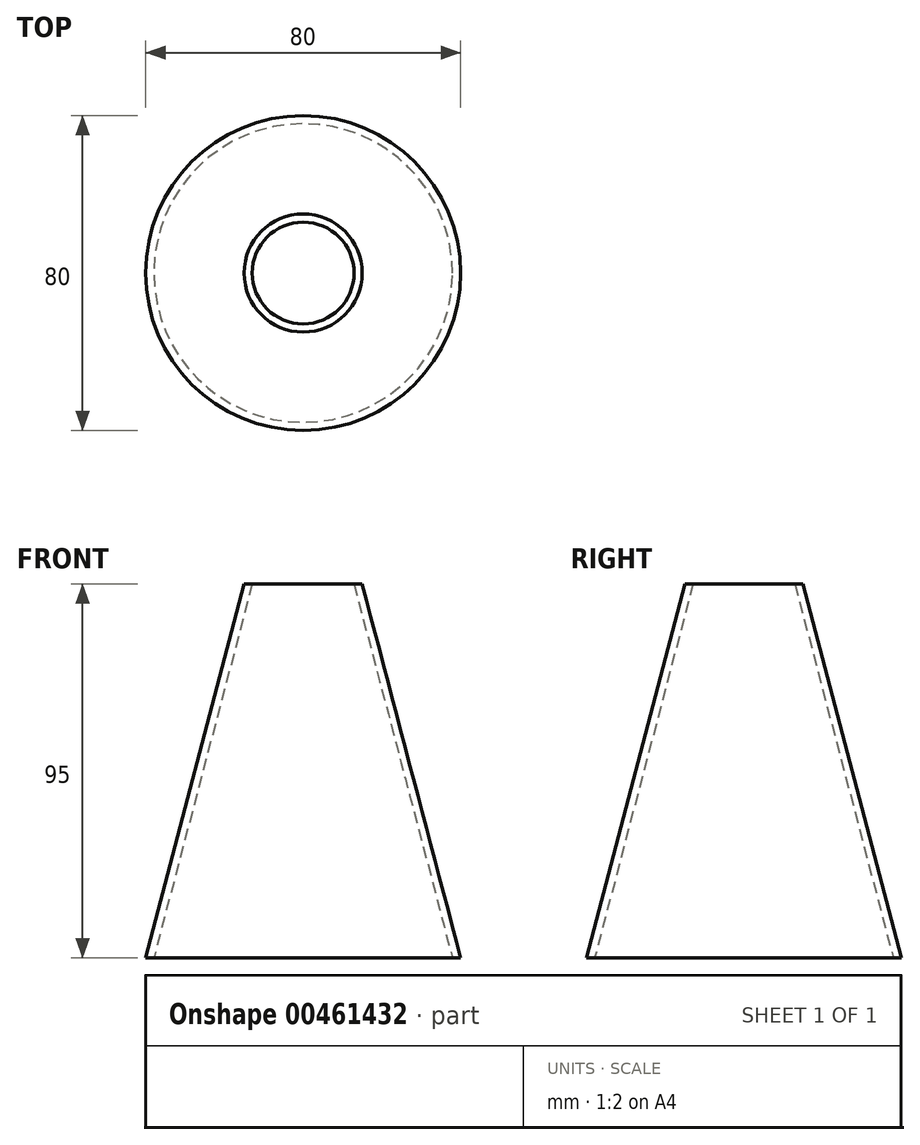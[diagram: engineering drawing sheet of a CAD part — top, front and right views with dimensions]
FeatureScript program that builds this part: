
annotation { "Feature Type Name" : "Feature", "Feature Type Description" : "" }
export const myFeature = defineFeature(function(context is Context, id is Id, definition is map)
    precondition{}
    {
        {
            var Q0;
            Q0=qCreatedBy(makeId("Top.planeOp"),FACE);
            var sketch = newSketch(context, id + "F0", { "sketchPlane" : qUnion([Q0])});
            skCircle(sketch, "E0", {"center": v(0, 0) * mm, "radius": 40 * mm});
            skSolve(sketch);
        }
        {
            var Q0;
            Q0=qCreatedBy(makeId("Top.planeOp"),FACE);
            cPlane(context, id + "F1", {"entities" : qUnion([Q0]), "cplaneType" : CPlaneType.OFFSET, "offset" : 95 * mm, "width" : 150 * mm, "height" : 150 * mm});
        }
        {
            var Q0;
            Q0=qCreatedBy(id+"F1.planeOp",FACE);
            var sketch = newSketch(context, id + "F2", { "sketchPlane" : qUnion([Q0])});
            skCircle(sketch, "E1", {"center": v(0, 0) * mm, "radius": 15 * mm});
            skSolve(sketch);
        }
        {
            var Q0;
            Q0=makeQuery(id+"F0.imprint","IMPRINT",FACE,{"disambiguationData":[TD([[makeQuery(id+"F0.imprint","IMPRINT",EDGE,{"derivedFrom":sQuery(id+"F0.wireOp",EDGE,"E0")}),1.0]])]});
            var Q1;
            Q1=makeQuery(id+"F2.imprint","IMPRINT",FACE,{"disambiguationData":[TD([[makeQuery(id+"F2.imprint","IMPRINT",EDGE,{"derivedFrom":sQuery(id+"F2.wireOp",EDGE,"E1")}),1.0]])]});
            loft(context, id + "F3", {"sheetProfilesArray" : [{ "sheetProfileEntities" : qUnion([Q0]) }, { "sheetProfileEntities" : qUnion([Q1]) }]});
        }
        {
            var Q0;
            Q0=makeQuery(id+"F3.opLoft","CAP_FACE",FACE,{"disambiguationData":[OSD([makeQuery(id+"F2.imprint","IMPRINT",FACE,{"disambiguationData":[TD([[makeQuery(id+"F2.imprint","IMPRINT",EDGE,{"derivedFrom":sQuery(id+"F2.wireOp",EDGE,"E1")}),1.0]])]})])],"isStart":true});
            var Q1;
            Q1=makeQuery(id+"F3.opLoft","CAP_FACE",FACE,{"disambiguationData":[OSD([makeQuery(id+"F0.imprint","IMPRINT",FACE,{"disambiguationData":[TD([[makeQuery(id+"F0.imprint","IMPRINT",EDGE,{"derivedFrom":sQuery(id+"F0.wireOp",EDGE,"E0")}),1.0]])]})])],"isStart":true});
            var Q2;
            Q2=makeQuery(id+"F3.opLoft","SWEPT_BODY",BODY,{"disambiguationData":[OSD([makeQuery(id+"F0.imprint","IMPRINT",FACE,{"disambiguationData":[TD([[makeQuery(id+"F0.imprint","IMPRINT",EDGE,{"derivedFrom":sQuery(id+"F0.wireOp",EDGE,"E0")}),1.0]])]}),makeQuery(id+"F2.imprint","IMPRINT",FACE,{"disambiguationData":[TD([[makeQuery(id+"F2.imprint","IMPRINT",EDGE,{"derivedFrom":sQuery(id+"F2.wireOp",EDGE,"E1")}),1.0]])]})])]});
            shell(context, id + "F4", {"entities" : qUnion([Q0, Q1]), "parts" : qUnion([Q2]), "thickness" : 2 * mm});
        }
    });
